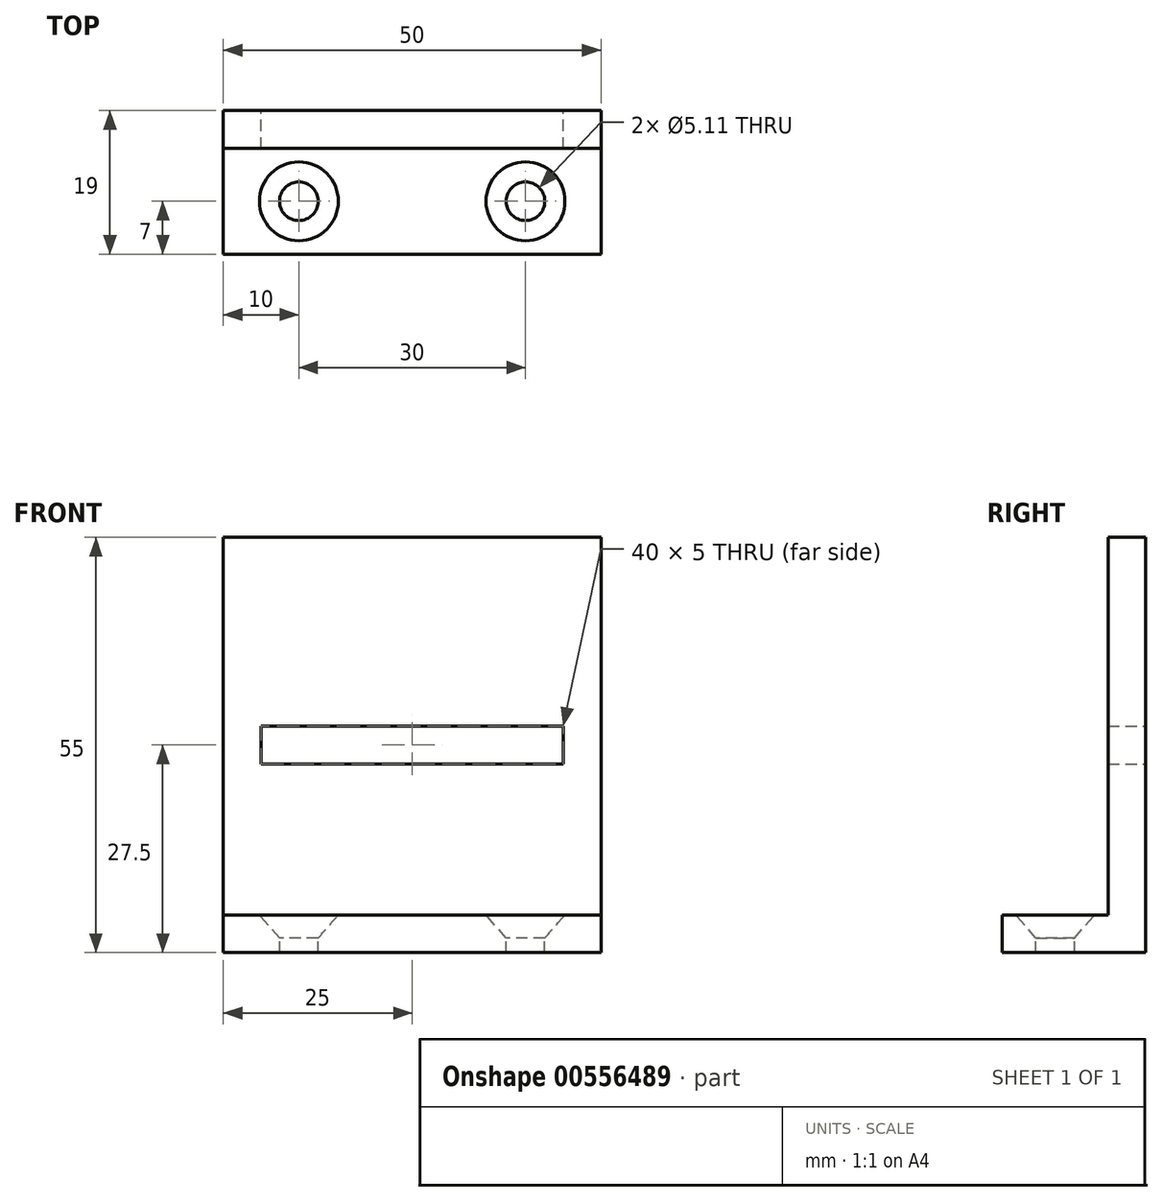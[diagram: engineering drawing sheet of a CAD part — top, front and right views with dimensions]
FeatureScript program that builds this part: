
annotation { "Feature Type Name" : "Feature", "Feature Type Description" : "" }
export const myFeature = defineFeature(function(context is Context, id is Id, definition is map)
    precondition{}
    {
        {
            var Q0;
            Q0=qCreatedBy(makeId("Top.planeOp"),FACE);
            var sketch = newSketch(context, id + "F0", { "sketchPlane" : qUnion([Q0])});
            skLineSegment(sketch, "E0.bottom", {"start": v(15, 7.5) * mm, "end": v(-15, 7.5) * mm});
            skLineSegment(sketch, "E0.top", {"start": v(15, -7.5) * mm, "end": v(-15, -7.5) * mm});
            skLineSegment(sketch, "E0.left", {"start": v(15, 7.5) * mm, "end": v(15, -7.5) * mm});
            skLineSegment(sketch, "E0.right", {"start": v(-15, 7.5) * mm, "end": v(-15, -7.5) * mm});
            skPoint(sketch, "E0.middle", {"position": v(0, 0) * mm});
            skSolve(sketch);
        }
        {
            var Q0;
            Q0=makeQuery(id+"F0.imprint","IMPRINT",FACE,{"disambiguationData":[TD([[makeQuery(id+"F0.imprint","IMPRINT",EDGE,{"derivedFrom":sQuery(id+"F0.wireOp",EDGE,"E0.bottom")}),1.0]])]});
            extrude(context, id + "F1", {"entities" : qUnion([Q0]), "depth" : 5 * mm, "offsetDistance" : 25 * mm});
        }
        {
            var Q0;
            Q0=makeQuery(id+"F1.opExtrude","CAP_FACE",FACE,{"disambiguationData":[OSD([sQuery(id+"F0.wireOp",EDGE,"E0.bottom"),sQuery(id+"F0.wireOp",EDGE,"E0.top"),sQuery(id+"F0.wireOp",EDGE,"E0.left"),sQuery(id+"F0.wireOp",EDGE,"E0.right")])],"isStart":false});
            var sketch = newSketch(context, id + "F2", { "sketchPlane" : qUnion([Q0])});
            skLineSegment(sketch, "E1.bottom", {"start": v(-15, 7.5) * mm, "end": v(15, 7.5) * mm});
            skLineSegment(sketch, "E1.top", {"start": v(-15, 2.5) * mm, "end": v(15, 2.5) * mm});
            skLineSegment(sketch, "E1.left", {"start": v(-15, 7.5) * mm, "end": v(-15, 2.5) * mm});
            skLineSegment(sketch, "E1.right", {"start": v(15, 7.5) * mm, "end": v(15, 2.5) * mm});
            skSolve(sketch);
        }
        {
            var Q0;
            Q0=makeQuery(id+"F2.imprint","IMPRINT",FACE,{"disambiguationData":[TD([[makeQuery(id+"F2.imprint","IMPRINT",EDGE,{"derivedFrom":sQuery(id+"F2.wireOp",EDGE,"E1.bottom")}),1.0]])]});
            extrude(context, id + "F3", {"entities" : qUnion([Q0]), "operationType" : NewBodyOperationType.ADD, "depth" : 50 * mm, "offsetDistance" : 25 * mm});
        }
        {
            var Q0;
            Q0=makeQuery(id+"F3.boolean.opBoolean","MERGE",FACE,{"derivedFrom":[makeQuery(id+"F1.opExtrude","SWEPT_FACE",FACE,{"disambiguationData":[OSD([sQuery(id+"F0.wireOp",EDGE,"E0.right")])]}),makeQuery(id+"F3.opExtrude","SWEPT_FACE",FACE,{"disambiguationData":[OSD([sQuery(id+"F2.wireOp",EDGE,"E1.left")])]})]});
            extrude(context, id + "F4", {"entities" : qUnion([Q0]), "operationType" : NewBodyOperationType.ADD, "depth" : 10 * mm, "offsetDistance" : 25 * mm});
        }
        {
            var Q0;
            Q0=makeQuery(id+"F3.boolean.opBoolean","MERGE",FACE,{"derivedFrom":[makeQuery(id+"F1.opExtrude","SWEPT_FACE",FACE,{"disambiguationData":[OSD([sQuery(id+"F0.wireOp",EDGE,"E0.left")])]}),makeQuery(id+"F3.opExtrude","SWEPT_FACE",FACE,{"disambiguationData":[OSD([sQuery(id+"F2.wireOp",EDGE,"E1.right")])]})]});
            extrude(context, id + "F5", {"entities" : qUnion([Q0]), "operationType" : NewBodyOperationType.ADD, "depth" : 10 * mm, "offsetDistance" : 25 * mm});
        }
        {
            var Q0;
            {var subQ0=sQuery(id+"F0.wireOp",EDGE,"E0.top");Q0=makeQuery(id+"F5.boolean.opBoolean","MERGE",FACE,{"derivedFrom":[makeQuery(id+"F4.boolean.opBoolean","MERGE",FACE,{"derivedFrom":[makeQuery(id+"F1.opExtrude","SWEPT_FACE",FACE,{"disambiguationData":[OSD([subQ0])]}),makeQuery(id+"F4.opExtrude","SWEPT_FACE",FACE,{"disambiguationData":[OSD([subQ0,sQuery(id+"F0.wireOp",EDGE,"E0.right")])]})]}),makeQuery(id+"F5.opExtrude","SWEPT_FACE",FACE,{"disambiguationData":[OSD([subQ0,sQuery(id+"F0.wireOp",EDGE,"E0.left")])]})]});}
            extrude(context, id + "F6", {"entities" : qUnion([Q0]), "operationType" : NewBodyOperationType.ADD, "depth" : 4 * mm, "offsetDistance" : 25 * mm});
        }
        {
            var Q0;
            {var subQ0=sQuery(id+"F0.wireOp",EDGE,"E0.left");var subQ1=sQuery(id+"F0.wireOp",EDGE,"E0.top");var subQ2=sQuery(id+"F0.wireOp",EDGE,"E0.right");Q0=makeQuery(id+"F6.boolean.opBoolean","MERGE",FACE,{"derivedFrom":[makeQuery(id+"F5.boolean.opBoolean","MERGE",FACE,{"derivedFrom":[makeQuery(id+"F4.boolean.opBoolean","MERGE",FACE,{"derivedFrom":[makeQuery(id+"F1.opExtrude","CAP_FACE",FACE,{"disambiguationData":[OSD([sQuery(id+"F0.wireOp",EDGE,"E0.bottom"),subQ1,subQ0,subQ2])],"isStart":false}),makeQuery(id+"F4.opExtrude","SWEPT_FACE",FACE,{"disambiguationData":[OSD([subQ2]),TDD([makeQuery(id+"F1.opExtrude","CAP_EDGE",EDGE,{"disambiguationData":[OSD([subQ2])],"isStart":false})])]})]}),makeQuery(id+"F5.opExtrude","SWEPT_FACE",FACE,{"disambiguationData":[OSD([subQ0]),TDD([makeQuery(id+"F1.opExtrude","CAP_EDGE",EDGE,{"disambiguationData":[OSD([subQ0])],"isStart":false})])]})]}),makeQuery(id+"F6.opExtrude","SWEPT_FACE",FACE,{"disambiguationData":[OSD([subQ1,subQ0,subQ2]),TDD([makeQuery(id+"F5.boolean.opBoolean","MERGE",EDGE,{"derivedFrom":[makeQuery(id+"F4.boolean.opBoolean","MERGE",EDGE,{"derivedFrom":[makeQuery(id+"F1.opExtrude","CAP_EDGE",EDGE,{"disambiguationData":[OSD([subQ1])],"isStart":false}),makeQuery(id+"F4.opExtrude","SWEPT_EDGE",EDGE,{"disambiguationData":[OSD([subQ1,subQ2]),TDD([makeQuery(id+"F1.opExtrude","CAP_VERTEX",VERTEX,{"disambiguationData":[OSD([subQ1,subQ2])],"isStart":false})])]})]}),makeQuery(id+"F5.opExtrude","SWEPT_EDGE",EDGE,{"disambiguationData":[OSD([subQ1,subQ0]),TDD([makeQuery(id+"F1.opExtrude","CAP_VERTEX",VERTEX,{"disambiguationData":[OSD([subQ1,subQ0])],"isStart":false})])]})]})])]})]});}
            var sketch = newSketch(context, id + "F7", { "sketchPlane" : qUnion([Q0])});
            skPoint(sketch, "E2", {"position": v(-15, -4.5) * mm});
            skPoint(sketch, "E3", {"position": v(15, -4.5) * mm});
            skSolve(sketch);
        }
        {
            var Q0;
            Q0=sQuery(id+"F7.wireOp",VERTEX,"E3");
            var Q1;
            Q1=sQuery(id+"F7.wireOp",VERTEX,"E2");
            var Q2;
            Q2=makeQuery(id+"F1.opExtrude","SWEPT_BODY",BODY,{"disambiguationData":[OSD([sQuery(id+"F0.wireOp",EDGE,"E0.bottom"),sQuery(id+"F0.wireOp",EDGE,"E0.top"),sQuery(id+"F0.wireOp",EDGE,"E0.left"),sQuery(id+"F0.wireOp",EDGE,"E0.right")])]});
            hole(context, id + "F8", {"style" : HoleStyle.C_SINK, "endStyle" : HoleEndStyle.BLIND, "standardTappedOrClearance" : lookupTablePath({ "standard" : "ANSI", "fit" : "Normal (ASME)", "size" : "#10", "type" : "Clearance" }), "standardBlindInLast" : lookupTablePath({ "fit" : "Free", "standard" : "ANSI", "size" : "#10", "type" : "Clearance" }), "holeDiameter" : 5.1 * mm, "cSinkDiameter" : 10.44 * mm, "cSinkAngle" : 82 * degree, "holeDepth" : 10 * mm, "isTappedThrough" : true, "tappedDepth" : 1 * mm, "tapClearance" : 3, "locations" : qUnion([Q0, Q1]), "scope" : qUnion([Q2])});
        }
        {
            var Q0;
            {var subQ0=sQuery(id+"F2.wireOp",EDGE,"E1.bottom");var subQ1=sQuery(id+"F0.wireOp",EDGE,"E0.bottom");Q0=makeQuery(id+"F5.boolean.opBoolean","MERGE",FACE,{"derivedFrom":[makeQuery(id+"F4.boolean.opBoolean","MERGE",FACE,{"derivedFrom":[makeQuery(id+"F3.boolean.opBoolean","MERGE",FACE,{"derivedFrom":[makeQuery(id+"F1.opExtrude","SWEPT_FACE",FACE,{"disambiguationData":[OSD([subQ1])]}),makeQuery(id+"F3.opExtrude","SWEPT_FACE",FACE,{"disambiguationData":[OSD([subQ0])]})]}),makeQuery(id+"F4.opExtrude","SWEPT_FACE",FACE,{"disambiguationData":[OSD([subQ1,sQuery(id+"F0.wireOp",EDGE,"E0.right"),subQ0,sQuery(id+"F2.wireOp",EDGE,"E1.left")])]})]}),makeQuery(id+"F5.opExtrude","SWEPT_FACE",FACE,{"disambiguationData":[OSD([subQ1,sQuery(id+"F0.wireOp",EDGE,"E0.left"),subQ0,sQuery(id+"F2.wireOp",EDGE,"E1.right")])]})]});}
            var sketch = newSketch(context, id + "F9", { "sketchPlane" : qUnion([Q0])});
            skPoint(sketch, "E4", {"position": v(0, 27.5) * mm});
            skPoint(sketch, "E5", {"position": v(20, 25) * mm});
            skPoint(sketch, "E6", {"position": v(-19.76, 34.35) * mm});
            skLineSegment(sketch, "E7.bottom", {"start": v(20, 25) * mm, "end": v(-20, 25) * mm});
            skLineSegment(sketch, "E7.top", {"start": v(20, 30) * mm, "end": v(-20, 30) * mm});
            skLineSegment(sketch, "E7.left", {"start": v(20, 25) * mm, "end": v(20, 30) * mm});
            skLineSegment(sketch, "E7.right", {"start": v(-20, 25) * mm, "end": v(-20, 30) * mm});
            skSolve(sketch);
        }
        {
            var Q0;
            Q0=makeQuery(id+"F9.imprint","IMPRINT",FACE,{"disambiguationData":[TD([[makeQuery(id+"F9.imprint","IMPRINT",EDGE,{"derivedFrom":sQuery(id+"F9.wireOp",EDGE,"E7.bottom")}),-1.0]])]});
            extrude(context, id + "F10", {"entities" : qUnion([Q0]), "operationType" : NewBodyOperationType.REMOVE, "endBound" : BoundingType.THROUGH_ALL, "oppositeDirection" : true, "depth" : 25 * mm, "offsetDistance" : 25 * mm});
        }
    });
